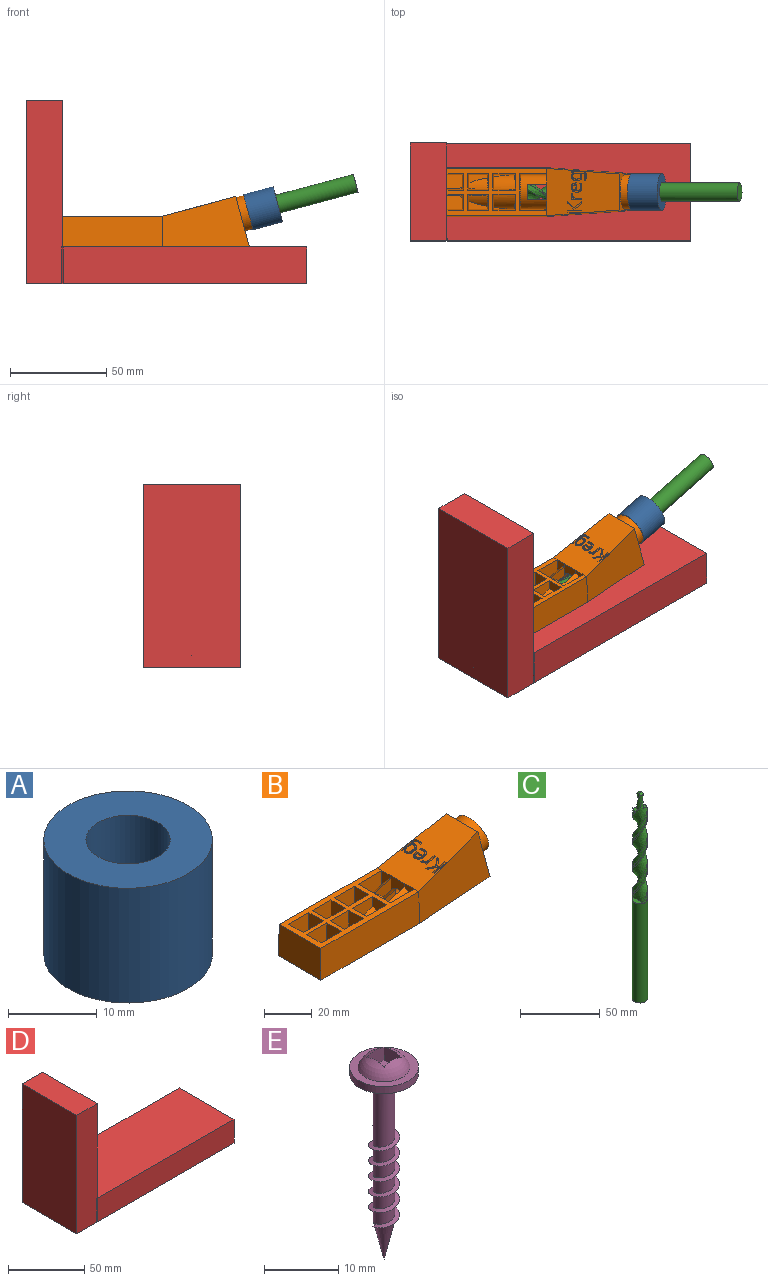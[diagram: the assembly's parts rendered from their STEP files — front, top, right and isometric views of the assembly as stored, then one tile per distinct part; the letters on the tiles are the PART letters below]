
ASSEMBLY  parts=5 mates=4
PART A: 4 faces, bbox 19.1x19.1x15.9 mm
  f0: cylinder r=4.76mm len=15.88mm, axis (0,0,1), area 475mm2, adj f2,f3
  f1: cylinder r=9.53mm len=19.05mm, axis (0,0,1), area 950.1mm2, adj f2,f3
  f2: plane 19.05x19.05mm, normal (0,0,-1), area 213.8mm2, adj f0,f1
  f3: plane 19.05x19.05mm, normal (0,0,1), area 213.8mm2, adj f0,f1
PART B: 150 faces, bbox 105.2x25.4x36.1 mm
  f0: plane 37.93x24.56mm, normal (-0.26,0,0.96), area 780.2mm2, adj f1,f7,f9,f10,f13,f22,f64,f68
  f1: plane 12.7x5.43mm, normal (-1,0,0.05), area 22.2mm2, adj f0,f3,f6,f19,f65
  f2: cylinder r=4.76mm len=87.51mm, axis (0.97,0,0.26), area 1767.9mm2, adj f5,f50,f57,f58,f59,f64,f65,f66
  f3: cylinder r=8.99mm len=18.15mm, axis (0.97,0,0.26), area 307.9mm2, adj f1,f6,f19,f20,f21,f22,f23,f65
  f4: plane 21.56x9.57mm, normal (0,0,-1), area 129.4mm2, adj f13,f60,f61,f62
  f5: plane 103.38x25.4mm, normal (0,0,-1), area 1928.3mm2, adj f2,f8,f9,f10,f11,f12,f13,f57
  f6: plane 5.31x0.32mm, normal (0,0,1), area 0.7mm2, adj f1,f3,f19
  f7: plane 57.99x24.56mm, normal (0,0,1), area 563.5mm2, adj f0,f8,f11,f12,f14,f15,f16,f17
  f8: plane 25.4x15.98mm, normal (-1,0,0.03), area 399.3mm2, adj f5,f7,f11,f12
  f9: plane 44.97x26.29mm, normal (0.07,-1,0.03), area 896.5mm2, adj f0,f5,f12,f13
  f10: plane 44.97x26.29mm, normal (0.07,1,0.03), area 896.5mm2, adj f0,f5,f11,f13
  f11: plane 58.42x15.98mm, normal (0,1,0.03), area 930.2mm2, adj f5,f7,f8,f10
  f12: plane 58.42x15.98mm, normal (0,-1,0.03), area 930.2mm2, adj f5,f7,f8,f9
  f13: plane 26.29x19.05mm, normal (0.97,0,0.26), area 244.1mm2, adj f0,f4,f5,f9,f10,f49,f60
  f14: plane 12.7x11.94mm, normal (0,-1,0.05), area 143.4mm2, adj f7,f15,f17,f18
  f15: plane 12.7x8.51mm, normal (1,0,0.05), area 99.7mm2, adj f7,f14,f16,f18
  f16: plane 12.7x11.94mm, normal (0,1,0.05), area 143.1mm2, adj f7,f15,f17,f18,f56
  f17: plane 12.72x8.53mm, normal (-1,0,0.05), area 99.5mm2, adj f7,f14,f16,f18,f56
  f18: plane 10.61x7.18mm, normal (0,0,1), area 75.1mm2, adj f14,f15,f16,f17,f56
  f19: plane 14.06x12.7mm, normal (0,-1,0.05), area 157.9mm2, adj f1,f3,f6,f7,f20
  f20: plane 19.11x12.14mm, normal (1,0,0.05), area 115.5mm2, adj f3,f7,f19,f21
  f21: plane 14.06x12.7mm, normal (0,1,0.05), area 157.9mm2, adj f3,f7,f20,f22,f23
  f22: plane 12.7x5.43mm, normal (-1,0,0.05), area 22.2mm2, adj f0,f3,f21,f23,f67
  f23: plane 5.31x0.32mm, normal (0,0,1), area 0.7mm2, adj f3,f21,f22
  f24: plane 12.7x8.51mm, normal (1,0,0.05), area 79.8mm2, adj f7,f25,f27,f28,f55
  f25: plane 12.7x11.94mm, normal (0,1,0.05), area 143.4mm2, adj f7,f24,f26,f28
  f26: plane 12.7x8.51mm, normal (-1,0,0.05), area 58.7mm2, adj f7,f25,f27,f28,f55
  f27: plane 11.95x7.95mm, normal (0,-1,0.05), area 74.7mm2, adj f7,f24,f26,f55
  f28: plane 10.61x0.95mm, normal (0,0,1), area 4.3mm2, adj f24,f25,f26,f55
  f29: plane 12.7x10.92mm, normal (0,1,0.05), area 130.4mm2, adj f7,f30,f32,f33
  f30: plane 12.7x8.51mm, normal (-1,0,0.05), area 85mm2, adj f7,f29,f31,f33,f54
  f31: plane 11.42x10.93mm, normal (0,-1,0.05), area 105mm2, adj f7,f30,f32,f54
  f32: plane 12.7x8.51mm, normal (1,0,0.05), area 97.4mm2, adj f7,f29,f31,f33,f54
  f33: plane 9.59x4.06mm, normal (0,0,1), area 24.9mm2, adj f29,f30,f32,f54
  f34: plane 12.7x11.94mm, normal (0,1,0.05), area 143.4mm2, adj f7,f35,f37,f38
  f35: plane 12.72x8.53mm, normal (-1,0,0.05), area 99.5mm2, adj f7,f34,f36,f38,f53
  f36: plane 12.7x11.94mm, normal (0,-1,0.05), area 143.1mm2, adj f7,f35,f37,f38,f53
  f37: plane 12.7x8.51mm, normal (1,0,0.05), area 99.7mm2, adj f7,f34,f36,f38
  f38: plane 10.61x7.18mm, normal (0,0,1), area 75.1mm2, adj f34,f35,f36,f37,f53
  f39: plane 12.7x11.94mm, normal (0,-1,0.05), area 143.4mm2, adj f7,f40,f42,f43
  f40: plane 12.7x8.51mm, normal (1,0,0.05), area 79.8mm2, adj f7,f39,f41,f43,f52
  f41: plane 11.95x7.95mm, normal (0,1,0.05), area 74.7mm2, adj f7,f40,f42,f52
  f42: plane 12.7x8.51mm, normal (-1,0,0.05), area 58.7mm2, adj f7,f39,f41,f43,f52
  f43: plane 10.61x0.95mm, normal (0,0,1), area 4.3mm2, adj f39,f40,f42,f52
  f44: plane 12.7x10.92mm, normal (0,-1,0.05), area 130.4mm2, adj f7,f45,f47,f48
  f45: plane 12.7x8.51mm, normal (1,0,0.05), area 97.4mm2, adj f7,f44,f46,f48,f51
  f46: plane 11.42x10.93mm, normal (0,1,0.05), area 105mm2, adj f7,f45,f47,f51
  f47: plane 12.7x8.51mm, normal (-1,0,0.05), area 85mm2, adj f7,f44,f46,f48,f51
  f48: plane 9.59x4.06mm, normal (0,0,1), area 24.9mm2, adj f44,f45,f47,f51
  f49: cylinder r=8.99mm len=18.46mm, axis (-0.97,0,-0.26), area 236.8mm2, adj f13,f50
  f50: plane 17.98x17.37mm, normal (0.97,0,0.26), area 182.7mm2, adj f2,f49
  f51: cylinder r=8.99mm len=11.11mm, axis (0.97,0,0.26), area 55.1mm2, adj f45,f46,f47,f48
  f52: cylinder r=8.99mm len=14.15mm, axis (0.97,0,0.26), area 112.2mm2, adj f40,f41,f42,f43
  f53: cylinder r=8.99mm len=1.5mm, axis (0.97,0,0.26), area 1.1mm2, adj f35,f36,f38
  f54: cylinder r=8.99mm len=11.11mm, axis (0.97,0,0.26), area 55.1mm2, adj f30,f31,f32,f33
  f55: cylinder r=8.99mm len=14.15mm, axis (0.97,0,0.26), area 112.2mm2, adj f24,f26,f27,f28
  f56: cylinder r=8.99mm len=1.5mm, axis (0.97,0,0.26), area 1.1mm2, adj f16,f17,f18
  f57: plane 9.53x7.09mm, normal (-1,0,0), area 30.6mm2, adj f2,f5,f58,f59
  f58: plane 26.44x7.09mm, normal (0,1,0), area 93.7mm2, adj f2,f5,f57
  f59: plane 26.44x7.09mm, normal (0,-1,0), area 93.7mm2, adj f2,f5,f57
  f60: extruded ~21.97x9.58mm, area 70.2mm2, adj f4,f5,f13
  f61: plane 5.08x3.3mm, normal (-1,0,0), area 16.8mm2, adj f4,f62,f63
  f62: extruded ~12.32x5.08mm, area 128.5mm2, adj f4,f61,f63
  f63: plane 12.32x3.3mm, normal (0,0,-1), area 31.9mm2, adj f61,f62
  f64: plane 8.26x7.25mm, normal (-1,0,0), area 45.4mm2, adj f0,f2,f65,f67
  f65: plane 10.16x9.97mm, normal (0,-1,0), area 59.1mm2, adj f1,f2,f3,f64,f66
  f66: plane 8.26x6.85mm, normal (1,0,0), area 39.3mm2, adj f2,f3,f65,f67
  f67: plane 10.16x9.97mm, normal (0,1,0), area 59.1mm2, adj f2,f3,f22,f64,f66
  f68: plane 0.92x0.86mm, normal (0.04,1,0.01), area 0.5mm2, adj f0,f69,f96,f97
  f69: plane 0.79x0.41mm, normal (0,1,0), area 0.2mm2, adj f0,f68,f70,f97
  f70: extruded ~1.32x1.04mm, area 1mm2, adj f0,f69,f71,f97
  f71: extruded ~1.13x0.85mm, area 0.9mm2, adj f0,f70,f72,f97
  f72: extruded ~2.06x0.85mm, area 1.6mm2, adj f0,f71,f73,f97
  f73: plane 1.02x0.96mm, normal (0,1,0), area 0.6mm2, adj f0,f72,f74,f97
  f74: extruded ~2.01x0.83mm, area 1.6mm2, adj f0,f73,f75,f97
  f75: extruded ~1.89x0.89mm, area 1.6mm2, adj f0,f74,f76,f97
  f76: extruded ~1.95x1.21mm, area 1.5mm2, adj f0,f75,f77,f97
  f77: plane 5.69x2.23mm, normal (0,-1,0), area 4.3mm2, adj f0,f76,f78,f97
  f78: plane 0.74x0.73mm, normal (0.96,0,0.26), area 0.6mm2, adj f0,f77,f79,f97
  f79: plane 0.93x0.92mm, normal (0.16,0.99,0.04), area 0.6mm2, adj f0,f78,f80,f97
  f80: plane 0.74x0.2mm, normal (0.96,0,0.26), area 0mm2, adj f0,f79,f81,f97
  f81: extruded ~1.75x1.02mm, area 1.5mm2, adj f0,f80,f82,f97
  f82: extruded ~1.68x0.95mm, area 1.5mm2, adj f0,f81,f83,f97
  f83: extruded ~2.26x1.29mm, area 1.7mm2, adj f0,f82,f84,f97
  f84: extruded ~2.26x1.29mm, area 1.7mm2, adj f0,f83,f85,f97
  f85: extruded ~1.69x0.93mm, area 1.5mm2, adj f0,f84,f86,f97
  f86: extruded ~1.73x1.01mm, area 1.5mm2, adj f0,f85,f96,f97
  f87: extruded ~1.23x0.86mm, area 1mm2, adj f88,f95,f97,f98
  f88: extruded ~1.12x0.88mm, area 1mm2, adj f87,f89,f97,f98
  f89: extruded ~1.73x1.15mm, area 1.3mm2, adj f88,f90,f97,f98
  f90: extruded ~1.74x1.15mm, area 1.3mm2, adj f89,f91,f97,f98
  f91: extruded ~1.09x0.88mm, area 1mm2, adj f90,f92,f97,f98
  f92: extruded ~1.25x0.87mm, area 1.1mm2, adj f91,f93,f97,f98
  f93: extruded ~1.77x1.16mm, area 1.3mm2, adj f92,f94,f97,f98
  f94: plane 0.79x0.41mm, normal (0,1,0), area 0.2mm2, adj f93,f95,f97,f98
  f95: extruded ~1.61x1.12mm, area 1.2mm2, adj f87,f94,f97,f98
  f96: plane 0.74x0.2mm, normal (-0.96,0,-0.26), area 0mm2, adj f0,f68,f86,f97
  f97: plane 7.92x4.95mm, normal (-0.26,0,0.96), area 18.5mm2, adj f68,f69,f70,f71,f72,f73,f74,f75
  f98: plane 4.13x3.11mm, normal (-0.26,0,0.96), area 11.2mm2, adj f87,f88,f89,f90,f91,f92,f93,f94
  f99: extruded ~1.04x0.85mm, area 0.9mm2, adj f100,f118,f119,f149
  f100: extruded ~0.99x0.84mm, area 0.8mm2, adj f99,f101,f119,f149
  f101: extruded ~1.35x1.05mm, area 1mm2, adj f100,f102,f119,f149
  f102: plane 2.85x0.74mm, normal (0.96,0,0.26), area 2.2mm2, adj f101,f118,f119,f149
  f103: extruded ~1.97x0.94mm, area 1.7mm2, adj f0,f104,f117,f119
  f104: extruded ~0.96x0.76mm, area 0.7mm2, adj f0,f103,f105,f119
  f105: extruded ~0.87x0.81mm, area 0.7mm2, adj f0,f104,f106,f119
  f106: plane 0.98x0.95mm, normal (0,-1,0), area 0.6mm2, adj f0,f105,f107,f119
  f107: extruded ~0.94x0.82mm, area 0.8mm2, adj f0,f106,f108,f119
  f108: extruded ~0.85x0.76mm, area 0.7mm2, adj f0,f107,f109,f119
  f109: extruded ~1.3x0.87mm, area 1.1mm2, adj f0,f108,f110,f119
  f110: extruded ~1.6x1.11mm, area 1.2mm2, adj f0,f109,f111,f119
  f111: plane 3.83x0.74mm, normal (-0.96,0,-0.26), area 2.9mm2, adj f0,f110,f112,f119
  f112: plane 0.88x0.74mm, normal (0,-1,0), area 0.4mm2, adj f0,f111,f113,f119
  f113: extruded ~1.98x1.22mm, area 1.5mm2, adj f0,f112,f114,f119
  f114: extruded ~1.68x0.91mm, area 1.4mm2, adj f0,f113,f115,f119
  f115: extruded ~1.8x0.97mm, area 1.6mm2, adj f0,f114,f116,f119
  f116: extruded ~2.27x1.3mm, area 1.7mm2, adj f0,f115,f117,f119
  f117: extruded ~2.22x1.29mm, area 1.7mm2, adj f0,f103,f116,f119
  f118: extruded ~1.34x1.04mm, area 1mm2, adj f99,f102,f119,f149
  f119: plane 5.6x4.78mm, normal (-0.26,0,0.96), area 13.2mm2, adj f99,f100,f101,f102,f103,f104,f105,f106
  f120: extruded ~0.75x0.66mm, area 0.5mm2, adj f0,f121,f133,f134
  f121: extruded ~0.95x0.81mm, area 0.8mm2, adj f0,f120,f122,f134
  f122: extruded ~1.01x0.96mm, area 0.9mm2, adj f0,f121,f123,f134
  f123: plane 0.74x0.2mm, normal (0.96,0,0.26), area 0mm2, adj f0,f122,f124,f134
  f124: plane 1.19x1mm, normal (0.1,-1,0.03), area 0.8mm2, adj f0,f123,f125,f134
  f125: plane 0.75x0.74mm, normal (0.96,0,0.26), area 0.6mm2, adj f0,f124,f126,f134
  f126: plane 5.6x2.2mm, normal (0,1,0), area 4.3mm2, adj f0,f125,f127,f134
  f127: plane 0.92x0.74mm, normal (-0.96,0,-0.26), area 0.7mm2, adj f0,f126,f128,f134
  f128: plane 3.08x1.52mm, normal (0,-1,0), area 2.3mm2, adj f0,f127,f129,f134
  f129: extruded ~1.12x0.99mm, area 0.8mm2, adj f0,f128,f130,f134
  f130: extruded ~0.91x0.85mm, area 0.7mm2, adj f0,f129,f131,f134
  f131: extruded ~0.82x0.8mm, area 0.7mm2, adj f0,f130,f132,f134
  f132: extruded ~0.75x0.61mm, area 0.5mm2, adj f0,f131,f133,f134
  f133: plane 1.02x0.96mm, normal (-0.13,-0.99,-0.03), area 0.6mm2, adj f0,f120,f132,f134
  f134: plane 5.5x3.27mm, normal (-0.26,0,0.96), area 7mm2, adj f120,f121,f122,f123,f124,f125,f126,f127
  f135: plane 1.11x0.74mm, normal (-0.96,0,-0.26), area 0.8mm2, adj f0,f136,f147,f148
  f136: plane 4.26x3.07mm, normal (0.57,-0.81,0.15), area 4mm2, adj f0,f135,f137,f148
  f137: plane 3.33x2.95mm, normal (-0.65,-0.74,-0.18), area 3.3mm2, adj f0,f136,f138,f148
  f138: plane 1.1x0.74mm, normal (0.96,0,0.26), area 0.8mm2, adj f0,f137,f139,f148
  f139: plane 3.06x2.65mm, normal (0.64,0.75,0.17), area 3mm2, adj f0,f138,f140,f148
  f140: plane 0.92x0.88mm, normal (0.65,0.74,0.18), area 0.7mm2, adj f0,f139,f141,f148
  f141: plane 3.74x1.7mm, normal (0,-1,0), area 2.8mm2, adj f0,f140,f142,f148
  f142: plane 0.94x0.74mm, normal (0.96,0,0.26), area 0.7mm2, adj f0,f141,f143,f148
  f143: plane 7.39x2.69mm, normal (0,1,0), area 5.7mm2, adj f0,f142,f144,f148
  f144: plane 0.94x0.74mm, normal (-0.96,0,-0.26), area 0.7mm2, adj f0,f143,f145,f148
  f145: plane 2.99x1.49mm, normal (0,-1,0), area 2.2mm2, adj f0,f144,f146,f148
  f146: plane 0.91x0.84mm, normal (-0.73,-0.66,-0.2), area 0.8mm2, adj f0,f145,f147,f148
  f147: plane 3.63x2.64mm, normal (-0.58,0.8,-0.16), area 3.4mm2, adj f0,f135,f146,f148
  f148: plane 7.19x5.45mm, normal (-0.26,0,0.96), area 15.7mm2, adj f135,f136,f137,f138,f139,f140,f141,f142
  f149: plane 2.85x1.54mm, normal (-0.26,0,0.96), area 3.7mm2, adj f99,f100,f101,f102,f118
PART C: 21 faces, bbox 10.5x10.5x159.4 mm
  f0: plane 1.2x0.85mm, normal (0,0,1), area 0.5mm2, adj f1,f19,f20
  f1: bspline ~82.55x9.61mm, area 688.1mm2, adj f0,f3,f4,f5,f6,f7,f11,f15
  f2: bspline ~82.55x9.61mm, area 686.4mm2, adj f3,f4,f5,f8,f9,f13,f16,f17
  f3: cylinder r=2.14mm len=11.2mm, axis (0,0,1), area 32.2mm2, adj f1,f2,f17,f19
  f4: cylinder r=2.14mm len=11.46mm, axis (0,0,1), area 32.3mm2, adj f1,f2,f18,f20
  f5: cylinder r=4.76mm len=105.41mm, axis (0,0,-1), area 2326.1mm2, adj f1,f2,f7,f8,f10,f12,f14,f15
  f6: cylinder r=4.76mm len=1.75mm, axis (0,0,-1), area 1.1mm2, adj f1,f7,f17
  f7: cylinder r=4.76mm len=43.03mm, axis (0,0,-1), area 52.5mm2, adj f1,f5,f6,f12
  f8: cylinder r=4.76mm len=43.03mm, axis (0,0,-1), area 52.5mm2, adj f2,f5,f9,f10
  f9: cylinder r=4.76mm len=22.39mm, axis (0,0,-1), area 27.4mm2, adj f2,f8,f10,f18
  f10: bspline ~72.23x9.85mm, area 21.8mm2, adj f5,f8,f9,f11,f15,f18
  f11: bspline ~72.23x9.61mm, area 227.1mm2, adj f1,f10,f15,f18
  f12: bspline ~72.23x9.85mm, area 21.8mm2, adj f5,f7,f13,f16,f17
  f13: bspline ~72.23x9.61mm, area 227.1mm2, adj f2,f12,f16,f17
  f14: plane 9.53x9.53mm, normal (0,0,-1), area 71.3mm2, adj f5
  f15: plane 9.03x5.88mm, normal (0,0,1), area 21.9mm2, adj f1,f5,f10,f11
  f16: plane 9.03x5.88mm, normal (0,0,1), area 21.9mm2, adj f2,f5,f12,f13
  f17: plane 4.19x3.54mm, normal (0,0,1), area 8.7mm2, adj f1,f2,f3,f6,f12,f13
  f18: plane 4.19x3.54mm, normal (0,0,1), area 8.7mm2, adj f1,f2,f4,f9,f10,f11
  f19: plane 3.47x2.78mm, normal (-0.18,-0.51,0.84), area 5.8mm2, adj f0,f1,f2,f3,f20
  f20: plane 3.15x2.6mm, normal (-0.18,0.51,0.84), area 5.5mm2, adj f0,f1,f2,f4,f19
PART D: 13 faces, bbox 146.1x50.8x95.3 mm
  f0: plane 95.25x19.05mm, normal (0,-1,0), area 1807mm2, adj f3,f4,f5,f6,f9,f10
  f1: plane 126.6x19.05mm, normal (0,-1,0), area 2411.8mm2, adj f2,f6,f7,f12
  f2: plane 127x50.8mm, normal (0,0,1), area 6451.6mm2, adj f1,f3,f7,f8,f9
  f3: plane 76.2x50.8mm, normal (1,0,0), area 3871mm2, adj f0,f2,f4,f8
  f4: plane 50.8x19.05mm, normal (0,0,1), area 967.7mm2, adj f0,f3,f5,f8
  f5: plane 95.25x50.8mm, normal (-1,0,0), area 4838.7mm2, adj f0,f4,f6,f8
  f6: plane 146.05x50.8mm, normal (0,0,-1), area 7419.3mm2, adj f0,f1,f5,f7,f8,f11
  f7: plane 50.8x19.05mm, normal (1,0,0), area 967.7mm2, adj f1,f2,f6,f8
  f8: plane 146.05x95.25mm, normal (0,1,0), area 4233.9mm2, adj f2,f3,f4,f5,f6,f7
  f9: plane 2.25x0.79mm, normal (0,-0.17,-0.98), area 0.9mm2, adj f0,f2,f10,f12
  f10: plane 19.05x2.25mm, normal (0.98,-0.17,0), area 42.6mm2, adj f0,f9,f11,f12
  f11: plane 2.25x0.79mm, normal (0,-0.17,0.98), area 0.9mm2, adj f6,f10,f12
  f12: plane 19.05x2.25mm, normal (-0.98,-0.17,0), area 42.6mm2, adj f1,f9,f10,f11
PART E: 22 faces, bbox 10.9x10.9x35.2 mm
  f0: sphere r=3.81mm, area 37.8mm2, adj f9,f12,f13,f14,f15
  f1: cylinder r=1.46mm len=12.53mm, axis (0,0,1), area 102.5mm2, adj f2,f11,f17,f19,f21
  f2: cylinder r=1.46mm len=4.74mm, axis (0,0,1), area 20.2mm2, adj f1,f3,f19,f21
  f3: cylinder r=1.46mm len=4.74mm, axis (0,0,1), area 20.2mm2, adj f2,f4,f19,f21
  f4: cylinder r=1.46mm len=4.74mm, axis (0,0,1), area 20.2mm2, adj f3,f5,f19,f21
  f5: cylinder r=1.46mm len=4.74mm, axis (0,0,1), area 20.2mm2, adj f4,f6,f19,f21
  f6: cylinder r=1.46mm len=3.64mm, axis (0,0,1), area 18.1mm2, adj f5,f7,f8,f18,f19,f21
  f7: cylinder r=1.46mm len=2.8mm, axis (0,0,1), area 2.2mm2, adj f6,f8,f21
  f8: cone r=1.46mm half-angle=13deg, axis (0,0,1), area 29.9mm2, adj f6,f7,f20
  f9: plane 9.27x9.27mm, normal (0,0,1), area 29.2mm2, adj f0,f10
  f10: cylinder r=4.64mm len=9.27mm, axis (0,0,1), area 33.3mm2, adj f9,f11
  f11: plane 9.27x9.27mm, normal (0,0,-1), area 60.8mm2, adj f1,f10
  f12: plane 5.11x4.19mm, normal (0,-1,-0.05), area 8.2mm2, adj f0,f13,f15,f16
  f13: plane 5.11x4.19mm, normal (1,0,-0.05), area 8.2mm2, adj f0,f12,f14,f16
  f14: plane 5.11x4.19mm, normal (0,1,-0.05), area 8.2mm2, adj f0,f13,f15,f16
  f15: plane 3.96x3.04mm, normal (-1,0,-0.05), area 8.2mm2, adj f0,f12,f14,f16
  f16: plane 3.48x3.48mm, normal (0,0,1), area 12.1mm2, adj f12,f13,f14,f15
  f17: plane 0.64x0.34mm, normal (-1,0,0), area 0.1mm2, adj f1,f19,f21
  f18: plane 0.64x0.34mm, normal (0,1,0), area 0.1mm2, adj f6,f19,f20,f21
  f19: bspline ~14.99x4.84mm, area 43.3mm2, adj f1,f2,f3,f4,f5,f6,f17,f18
  f20: cylinder r=1.46mm len=0.59mm, axis (0,0,-1), area 0.1mm2, adj f8,f18,f21
  f21: bspline ~14.99x4.84mm, area 43.2mm2, adj f1,f2,f3,f4,f5,f6,f7,f17
PLACE A rot(axis=(0.79,0,-0.61),180deg) t=(96.5,25.4,37.22)mm
PLACE B t=(-6.35,25.4,19.05)mm
PLACE C rot(axis=(0.79,0,-0.61),180deg) t=(152.31,25.4,52.18)mm
PLACE D at identity fixed
PLACE E rot(axis=(0,1,0),75deg) t=(10.63,25.4,14.21)mm
MATE fastened E.f1 <-> C.f3  axis (-0.97,0,-0.26) through (10.63,25.4,14.21)mm
MATE fastened A.f1 <-> B.f49  axis (-0.97,0,-0.26) through (96.5,25.4,37.22)mm
MATE fastened A.f1 <-> C.f3  axis (-0.97,0,-0.26) through (96.5,25.4,37.22)mm
MATE fastened D.f2 <-> B.f5  axis (0,0,1) through (0,25.4,19.05)mm
